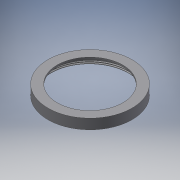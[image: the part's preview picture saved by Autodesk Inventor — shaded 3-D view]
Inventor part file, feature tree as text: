
AUTODESK INVENTOR PART (.ipt)
format: ipt  version: 2016 SP2 (Build 200236200, 236)  size: 300,032 bytes
history: native  units: mm
features: sketch x3, revolve x2, thread x1, other x1
ambient origin geometry x8: Origin, YZ Plane, XZ Plane, XY Plane, X Axis, Y Axis, Z Axis, Center Point
bodies: Volumenkörper1 (feature_tree), Volumenkörper3 (feature_tree)
feature tree (7):
  revolve  "Umdrehung1"
  thread  "Gewinde2"  [1 undecoded]
  revolve  "Umdrehung3"
  other  "Spirale2"
  sketch  "Skizze2"  dims[d1=3.0mm]
  sketch  "Skizze5"  dims[d3=7.0mm]
  sketch  "Skizze6"  dims[d4=8.0mm d5=2.0mm d6=50.0mm d7=0.0mm d8=90.0deg d18=60.0deg d29=3.0mm d30=10.0mm d31=0.0mm d32=60.0deg d33=0.320166mm d34=0.320166mm d37=2.0mm d39=60.0deg d41=0.0mm d42=2.002mm d43=7.0mm d44=10.0mm d45=0.0mm d46=0.0mm d47=0.0mm d48=0.0mm d49=0.0mm]
note: 1 required parameter value undecoded (feature->parameter linkage not recoverable at this tier; creation-order binding heuristic only, values carry confidence <= 0.55)
